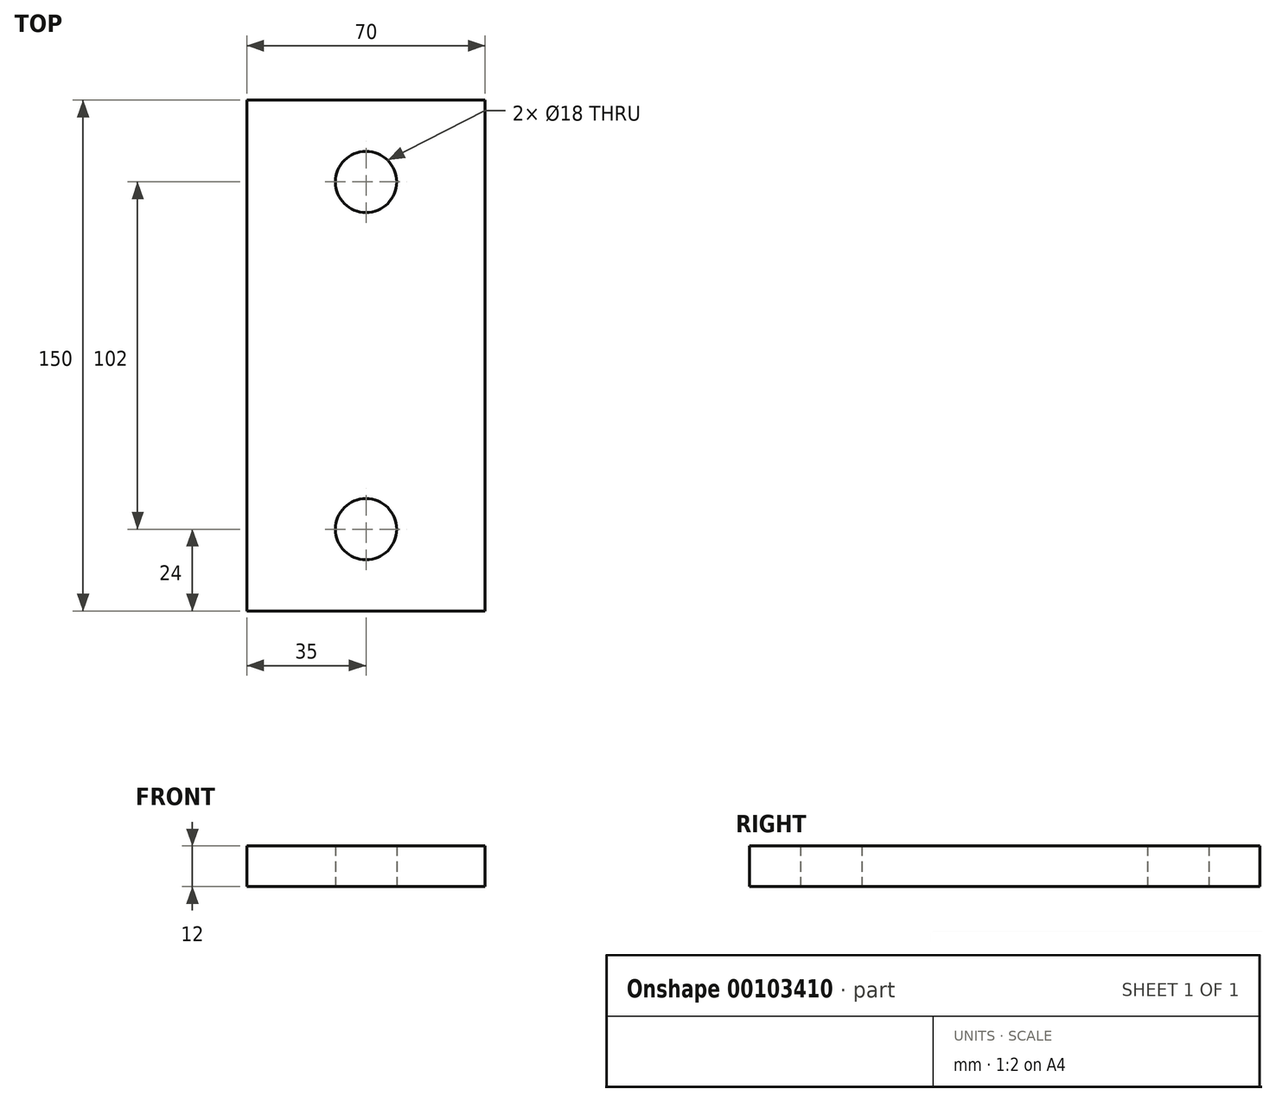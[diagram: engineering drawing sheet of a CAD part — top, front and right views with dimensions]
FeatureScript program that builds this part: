
annotation { "Feature Type Name" : "Feature", "Feature Type Description" : "" }
export const myFeature = defineFeature(function(context is Context, id is Id, definition is map)
    precondition{}
    {
        {
            var Q0;
            Q0=qCreatedBy(makeId("Top.planeOp"),FACE);
            var sketch = newSketch(context, id + "F0", { "sketchPlane" : qUnion([Q0])});
            skLineSegment(sketch, "E0.bottom", {"start": v(-35, 75) * mm, "end": v(35, 75) * mm});
            skLineSegment(sketch, "E0.top", {"start": v(-35, -75) * mm, "end": v(35, -75) * mm});
            skLineSegment(sketch, "E0.left", {"start": v(-35, 75) * mm, "end": v(-35, -75) * mm});
            skLineSegment(sketch, "E0.right", {"start": v(35, 75) * mm, "end": v(35, -75) * mm});
            skPoint(sketch, "E1", {"position": v(-35, 0) * mm});
            skPoint(sketch, "E2", {"position": v(0, -75) * mm});
            skSolve(sketch);
        }
        {
            var Q0;
            Q0=qSketchRegion(id+"F0",true);
            extrude(context, id + "F1", {"entities" : qUnion([Q0]), "depth" : 12 * mm, "offsetDistance" : 25 * mm});
        }
        {
            var Q0;
            Q0=makeQuery(id+"F1.opExtrude","CAP_FACE",FACE,{"disambiguationData":[OSD([sQuery(id+"F0.wireOp",EDGE,"E0.bottom"),sQuery(id+"F0.wireOp",EDGE,"E0.top"),sQuery(id+"F0.wireOp",EDGE,"E0.left"),sQuery(id+"F0.wireOp",EDGE,"E0.right")])],"isStart":true});
            var sketch = newSketch(context, id + "F2", { "sketchPlane" : qUnion([Q0])});
            skCircle(sketch, "E3", {"center": v(0, 51) * mm, "radius": 9 * mm});
            skCircle(sketch, "E4", {"center": v(0, -51) * mm, "radius": 9 * mm});
            skSolve(sketch);
        }
        {
            var Q0;
            Q0=qSketchRegion(id+"F2",true);
            extrude(context, id + "F3", {"entities" : qUnion([Q0]), "operationType" : NewBodyOperationType.REMOVE, "oppositeDirection" : true, "depth" : 25 * mm, "offsetDistance" : 25 * mm});
        }
        {
            var Q0;
            Q0=makeQuery(id+"F1.opExtrude","CAP_FACE",FACE,{"disambiguationData":[OSD([sQuery(id+"F0.wireOp",EDGE,"E0.bottom"),sQuery(id+"F0.wireOp",EDGE,"E0.top"),sQuery(id+"F0.wireOp",EDGE,"E0.left"),sQuery(id+"F0.wireOp",EDGE,"E0.right")])],"isStart":false});
            var sketch = newSketch(context, id + "F4", { "sketchPlane" : qUnion([Q0])});
            skLineSegment(sketch, "E5", {"start": v(0, -51) * mm, "end": v(0, 51) * mm});
            skPoint(sketch, "E6", {"position": v(0, 0) * mm});
            skPoint(sketch, "E7", {"position": v(0, -6) * mm});
            skSolve(sketch);
        }
    });
